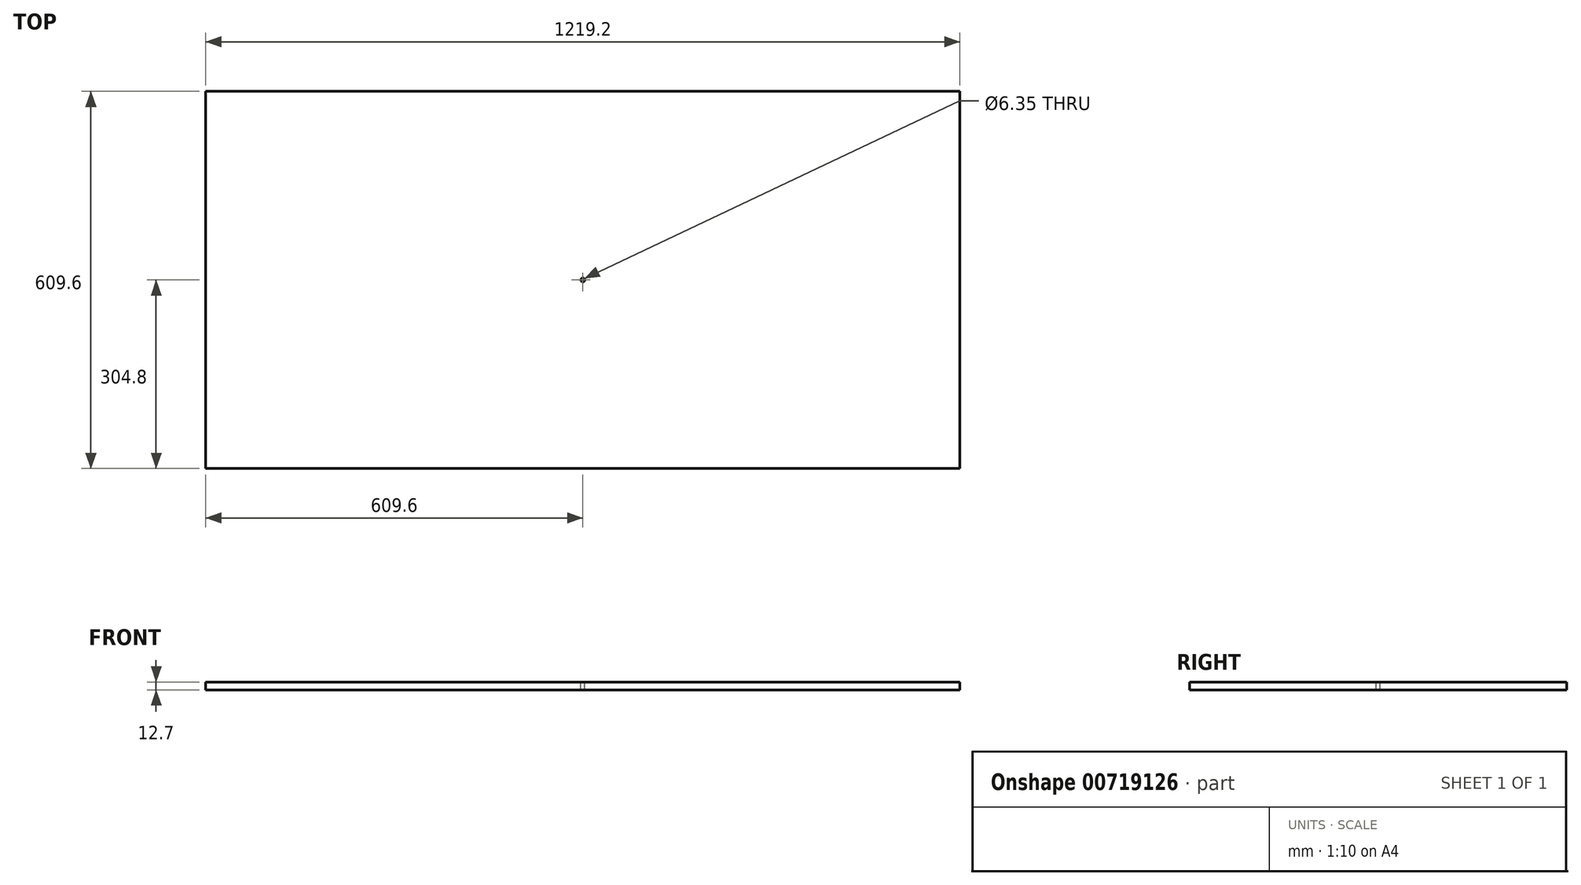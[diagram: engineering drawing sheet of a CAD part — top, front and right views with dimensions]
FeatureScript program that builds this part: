
annotation { "Feature Type Name" : "Feature", "Feature Type Description" : "" }
export const myFeature = defineFeature(function(context is Context, id is Id, definition is map)
    precondition{}
    {
        {
            var Q0;
            Q0=qCreatedBy(makeId("Top.planeOp"),FACE);
            var sketch = newSketch(context, id + "F0", { "sketchPlane" : qUnion([Q0])});
            skLineSegment(sketch, "E0.bottom", {"start": v(0, 0) * mm, "end": v(-1219.2, 0) * mm});
            skLineSegment(sketch, "E0.top", {"start": v(0, 609.6) * mm, "end": v(-1219.2, 609.6) * mm});
            skLineSegment(sketch, "E0.left", {"start": v(0, 0) * mm, "end": v(0, 609.6) * mm});
            skLineSegment(sketch, "E0.right", {"start": v(-1219.2, 0) * mm, "end": v(-1219.2, 609.6) * mm});
            skSolve(sketch);
        }
        {
            var Q0;
            Q0 = qSketchRegion(id + "F0", true);
            extrude(context, id + "F1", {"entities" : qUnion([Q0]), "depth" : 12.7 * mm, "offsetDistance" : 25.4 * mm});
        }
        {
            var Q0;
            Q0=makeQuery(id+"F1.opExtrude","CAP_FACE",FACE,{"disambiguationData":[OSD([sQuery(id+"F0.wireOp",EDGE,"E0.bottom"),sQuery(id+"F0.wireOp",EDGE,"E0.top"),sQuery(id+"F0.wireOp",EDGE,"E0.left"),sQuery(id+"F0.wireOp",EDGE,"E0.right")])],"isStart":false});
            var sketch = newSketch(context, id + "F2", { "sketchPlane" : qUnion([Q0])});
            skLineSegment(sketch, "E1", {"start": v(-1219.2, 0) * mm, "end": v(-609.6, 0) * mm});
            skLineSegment(sketch, "E2", {"start": v(-609.6, 0) * mm, "end": v(-609.6, 304.8) * mm});
            skCircle(sketch, "E3", {"center": v(-609.6, 304.8) * mm, "radius": 3.17 * mm});
            skSolve(sketch);
        }
        {
            var Q0;
            Q0 = qSketchRegion(id + "F2", true);
            extrude(context, id + "F3", {"entities" : qUnion([Q0]), "operationType" : NewBodyOperationType.REMOVE, "oppositeDirection" : true, "depth" : 25.4 * mm, "offsetDistance" : 25.4 * mm});
        }
    });
